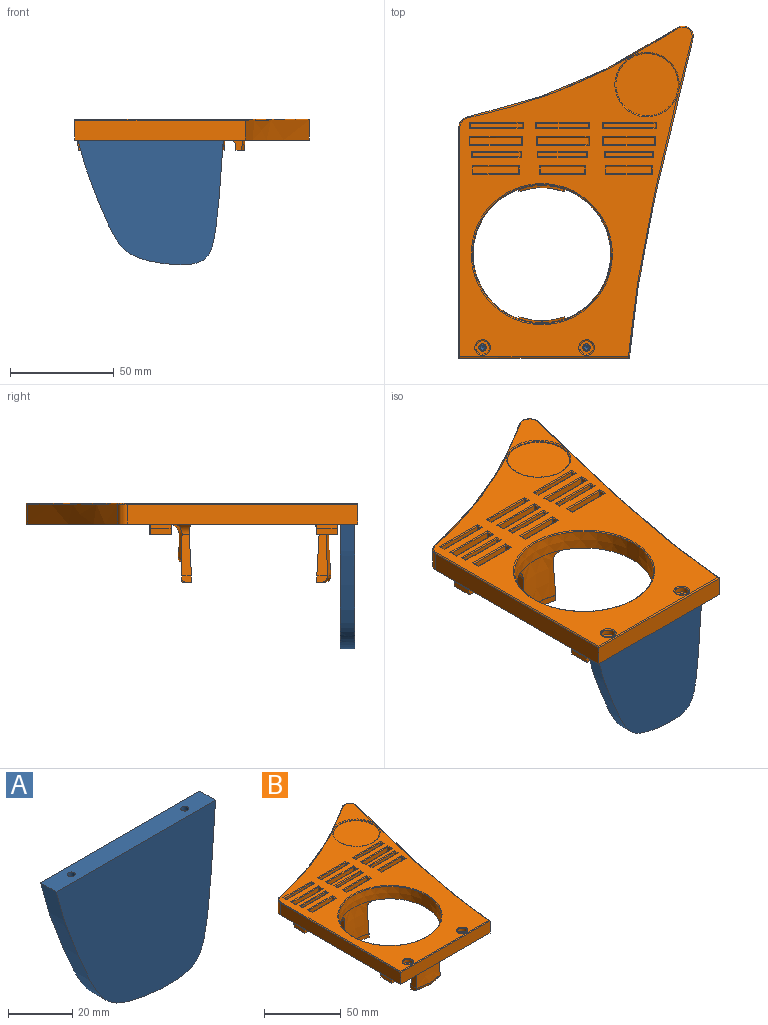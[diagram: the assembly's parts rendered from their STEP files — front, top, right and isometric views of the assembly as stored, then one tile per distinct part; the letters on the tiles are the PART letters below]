
ASSEMBLY  parts=2 mates=1
PART A: 8 faces, bbox 70x7x60.8 mm
  f0: plane 70x7mm, normal (0,0,1), area 480.2mm2, adj f1,f2,f3,f5,f7
  f1: extruded ~70x59.97mm, area 1100.6mm2, adj f0,f2,f3
  f2: plane 70x60.83mm, normal (0,-1,0), area 3319.7mm2, adj f0,f1
  f3: plane 70x60.83mm, normal (0,1,0), area 3319.7mm2, adj f0,f1
  f4: cone r=0mm half-angle=59deg, axis (0,0,1), area 5.7mm2, adj f5
  f5: cylinder r=1.25mm len=13.5mm, axis (0,0,1), area 106mm2, adj f0,f4
  f6: cone r=0mm half-angle=59deg, axis (0,0,1), area 5.7mm2, adj f7
  f7: cylinder r=1.25mm len=13.5mm, axis (0,0,1), area 106mm2, adj f0,f6
PART B: 196 faces, bbox 132.4x213.1x39.5 mm
  f0: plane 4.91x3.13mm, normal (-1,0,0), area 13.1mm2, adj f2,f38,f50,f51,f135
  f1: plane 4.91x3.13mm, normal (1,0,0), area 13.1mm2, adj f2,f40,f50,f51,f135
  f2: bspline ~23.11x4.73mm, area 41mm2, adj f0,f1,f51,f135
  f3: plane 158.85x111.92mm, normal (0,0,1), area 6703.7mm2, adj f138,f139,f140,f141,f142,f143,f144,f145
  f4: plane 12.78x3.46mm, normal (0,0,-1), area 1.2mm2, adj f36,f58
  f5: plane 163.02x112.92mm, normal (0,0,-1), area 8307.5mm2, adj f6,f7,f8,f9,f10,f11,f12,f13
  f6: plane 82.2x9.5mm, normal (0,-1,0), area 780.9mm2, adj f5,f7,f12,f142
  f7: extruded ~153.59x30.56mm, area 1489.5mm2, adj f5,f6,f8,f143
  f8: cylinder r=5mm len=9.5mm, axis (0,0,-1), area 113.5mm2, adj f5,f7,f9,f141
  f9: extruded ~101.41x43.16mm, area 1053.3mm2, adj f5,f8,f10,f139
  f10: cylinder r=5mm len=9.5mm, axis (0,0,-1), area 63.5mm2, adj f5,f9,f12,f138
  f11: cone r=33.11mm half-angle=2.3deg, axis (0,0,1), area 1993.2mm2, adj f5,f34,f39,f195
  f12: plane 111.04x9.5mm, normal (-1,0,0), area 1054.9mm2, adj f5,f6,f10,f140
  f13: plane 6x5mm, normal (0,-1,0), area 16.5mm2, adj f5,f14,f16,f17,f62,f64
  f14: plane 10x2mm, normal (-1,0,0), area 20mm2, adj f5,f13,f15,f64
  f15: plane 6x5mm, normal (0,1,0), area 16.5mm2, adj f5,f14,f16,f17,f62,f64
  f16: plane 10x2mm, normal (1,0,0), area 20mm2, adj f13,f15,f17,f62
  f17: plane 10x2.74mm, normal (0,0,-1), area 27.4mm2, adj f13,f15,f16,f64
  f18: plane 6x5mm, normal (0,-1,0), area 16.5mm2, adj f5,f19,f21,f22,f61,f63
  f19: plane 10x2mm, normal (-1,0,0), area 20mm2, adj f5,f18,f20,f63
  f20: plane 6x5mm, normal (0,1,0), area 16.5mm2, adj f5,f19,f21,f22,f61,f63
  f21: plane 10x2mm, normal (1,0,0), area 20mm2, adj f18,f20,f22,f61
  f22: plane 10x2.74mm, normal (0,0,-1), area 27.4mm2, adj f18,f20,f21,f63
  f23: plane 5.99x5mm, normal (-0.07,-1,0), area 16.5mm2, adj f5,f24,f26,f27,f60,f66
  f24: plane 9.98x2mm, normal (-1,0.07,0), area 20mm2, adj f23,f25,f27,f60
  f25: plane 5.99x5mm, normal (0.07,1,0), area 16.5mm2, adj f5,f24,f26,f27,f60,f66
  f26: plane 9.98x2mm, normal (1,-0.07,0), area 20mm2, adj f5,f23,f25,f66
  f27: plane 10.17x3.44mm, normal (0,0,-1), area 27.4mm2, adj f23,f24,f25,f66
  f28: plane 5.95x5mm, normal (-0.12,-0.99,0), area 16.5mm2, adj f5,f29,f31,f32,f59,f65
  f29: plane 9.92x2mm, normal (-0.99,0.12,0), area 20mm2, adj f28,f30,f32,f59
  f30: plane 5.95x5mm, normal (0.12,0.99,0), area 16.5mm2, adj f5,f29,f31,f32,f59,f65
  f31: plane 9.92x2mm, normal (0.99,-0.12,0), area 20mm2, adj f5,f28,f30,f65
  f32: plane 10.26x3.95mm, normal (0,0,-1), area 27.4mm2, adj f28,f29,f30,f65
  f33: plane 19.82x5.13mm, normal (1,0,0.04), area 84.6mm2, adj f34,f36,f45,f55
  f34: cone r=33.11mm half-angle=2.3deg, axis (0,0,1), area 547.4mm2, adj f11,f33,f35,f42,f43,f55,f57
  f35: plane 19.82x5.13mm, normal (-1,0,0.04), area 84.6mm2, adj f34,f36,f46,f57
  f36: cone r=35.98mm half-angle=2.3deg, axis (0,0,-1), area 426mm2, adj f4,f33,f35,f37,f56
  f37: plane 12.76x3.44mm, normal (0,0,-1), area 1.2mm2, adj f36,f58
  f38: plane 19.9x4.98mm, normal (-1,0,0.04), area 83mm2, adj f0,f39,f41,f52,f135,f136,f137
  f39: cone r=33.11mm half-angle=2.3deg, axis (0,0,1), area 547.4mm2, adj f11,f38,f40,f48,f49,f52,f54
  f40: plane 19.9x4.98mm, normal (1,0,0.04), area 83mm2, adj f1,f39,f41,f54,f135,f136,f137
  f41: cone r=35.98mm half-angle=2.3deg, axis (0,0,-1), area 254.5mm2, adj f38,f40,f53,f137
  f42: plane 11.32x2.27mm, normal (0,0,1), area 1.4mm2, adj f34,f44
  f43: plane 11.32x2.27mm, normal (0,0,1), area 1.4mm2, adj f34,f44
  f44: extruded ~21.97x3mm, area 67.1mm2, adj f42,f43,f45,f46,f47
  f45: plane 5.25x3.14mm, normal (1,0,0), area 13.4mm2, adj f33,f44,f47,f58
  f46: plane 5.24x3.13mm, normal (-1,0,0), area 13.4mm2, adj f35,f44,f47,f58
  f47: plane 21.98x3.78mm, normal (0,0,-1), area 42mm2, adj f44,f45,f46,f58
  f48: plane 11.32x2.27mm, normal (0,0,1), area 1.4mm2, adj f39,f50
  f49: plane 11.32x2.27mm, normal (0,0,1), area 1.4mm2, adj f39,f50
  f50: extruded ~21.97x3mm, area 67.1mm2, adj f0,f1,f48,f49,f51
  f51: plane 21.98x3.78mm, normal (0,0,-1), area 42mm2, adj f0,f1,f2,f50
  f52: cylinder r=5mm len=8.86mm, axis (0,1,0), area 49.5mm2, adj f5,f38,f39,f53
  f53: torus R=41.18mm, axis (0,0,1), area 196.2mm2, adj f5,f41,f52,f54
  f54: cylinder r=5mm len=8.86mm, axis (0,1,0), area 49.5mm2, adj f5,f39,f40,f53
  f55: cylinder r=5mm len=8.86mm, axis (0,-1,0), area 49.5mm2, adj f5,f33,f34,f56
  f56: torus R=41.18mm, axis (0,0,1), area 196.2mm2, adj f5,f36,f55,f57
  f57: cylinder r=5mm len=8.86mm, axis (0,-1,0), area 49.5mm2, adj f5,f34,f35,f56
  f58: bspline ~23.11x4.73mm, area 105.3mm2, adj f4,f37,f45,f46,f47
  f59: cylinder r=3mm len=10.29mm, axis (-0.12,-0.99,0), area 47.1mm2, adj f5,f28,f29,f30
  f60: cylinder r=3mm len=10.19mm, axis (-0.07,-1,0), area 47.1mm2, adj f5,f23,f24,f25
  f61: cylinder r=3mm len=10mm, axis (0,1,0), area 47.1mm2, adj f5,f18,f20,f21
  f62: cylinder r=3mm len=10mm, axis (0,1,0), area 47.1mm2, adj f5,f13,f15,f16
  f63: plane 10x3mm, normal (-1,0,-0.09), area 30.1mm2, adj f18,f19,f20,f22
  f64: plane 10x3mm, normal (-1,0,-0.09), area 30.1mm2, adj f13,f14,f15,f17
  f65: plane 9.96x3mm, normal (0.99,-0.12,-0.09), area 30.1mm2, adj f28,f30,f31,f32
  f66: plane 9.99x3mm, normal (0.99,-0.07,-0.09), area 30.1mm2, adj f23,f25,f26,f27
  f67: cylinder r=1.8mm len=7mm, axis (0,0,1), area 79.2mm2, adj f5,f68
  f68: plane 6.5x6.5mm, normal (0,0,1), area 23mm2, adj f67,f69
  f69: cylinder r=3.25mm len=6.5mm, axis (0,0,1), area 51.1mm2, adj f68,f193
  f70: cylinder r=1.8mm len=7mm, axis (0,0,1), area 79.2mm2, adj f5,f71
  f71: plane 6.5x6.5mm, normal (0,0,1), area 23mm2, adj f70,f72
  f72: cylinder r=3.25mm len=6.5mm, axis (0,0,1), area 51.1mm2, adj f71,f194
  f73: plane 7.5x2.15mm, normal (1,0,0), area 16.1mm2, adj f74,f76,f77,f190
  f74: plane 23x7.5mm, normal (0,1,0), area 172.5mm2, adj f73,f75,f77,f192
  f75: plane 7.5x2.15mm, normal (-1,0,0), area 16.1mm2, adj f74,f76,f77,f191
  f76: plane 23x7.5mm, normal (0,-1,0), area 172.5mm2, adj f73,f75,f77,f189
  f77: plane 23x2.15mm, normal (0,0,1), area 49.4mm2, adj f73,f74,f75,f76
  f78: plane 21.5x7.5mm, normal (0,-1,0), area 161.2mm2, adj f79,f81,f82,f146
  f79: plane 7.5x3.2mm, normal (1,0,0), area 24mm2, adj f78,f80,f82,f148
  f80: plane 21.5x7.5mm, normal (0,1,0), area 161.2mm2, adj f79,f81,f82,f147
  f81: plane 7.5x3.2mm, normal (-1,0,0), area 24mm2, adj f78,f80,f82,f145
  f82: plane 21.5x3.2mm, normal (0,0,1), area 68.8mm2, adj f78,f79,f80,f81
  f83: plane 25x7.5mm, normal (0,-1,0), area 187.5mm2, adj f84,f86,f87,f150
  f84: plane 7.5x2.23mm, normal (1,0,0), area 16.7mm2, adj f83,f85,f87,f152
  f85: plane 25x7.5mm, normal (0,1,0), area 187.5mm2, adj f84,f86,f87,f151
  f86: plane 7.5x2.23mm, normal (-1,0,0), area 16.7mm2, adj f83,f85,f87,f149
  f87: plane 25x2.23mm, normal (0,0,1), area 55.8mm2, adj f83,f84,f85,f86
  f88: plane 24.5x7.5mm, normal (0,-1,0), area 183.7mm2, adj f89,f91,f92,f154
  f89: plane 7.5x3.46mm, normal (1,0,0), area 26mm2, adj f88,f90,f92,f156
  f90: plane 24.5x7.5mm, normal (0,1,0), area 183.7mm2, adj f89,f91,f92,f155
  f91: plane 7.5x3.46mm, normal (-1,0,0), area 26mm2, adj f88,f90,f92,f153
  f92: plane 24.5x3.46mm, normal (0,0,1), area 84.8mm2, adj f88,f89,f90,f91
  f93: plane 24.5x7.5mm, normal (0,-1,0), area 183.7mm2, adj f94,f96,f97,f185
  f94: plane 7.5x3.46mm, normal (1,0,0), area 26mm2, adj f93,f95,f97,f186
  f95: plane 24.5x7.5mm, normal (0,1,0), area 183.7mm2, adj f94,f96,f97,f188
  f96: plane 7.5x3.46mm, normal (-1,0,0), area 26mm2, adj f93,f95,f97,f187
  f97: plane 24.5x3.46mm, normal (0,0,1), area 84.8mm2, adj f93,f94,f95,f96
  f98: plane 25x7.5mm, normal (0,-1,0), area 187.5mm2, adj f99,f101,f102,f182
  f99: plane 7.5x2.23mm, normal (1,0,0), area 16.7mm2, adj f98,f100,f102,f184
  f100: plane 25x7.5mm, normal (0,1,0), area 187.5mm2, adj f99,f101,f102,f183
  f101: plane 7.5x2.23mm, normal (-1,0,0), area 16.7mm2, adj f98,f100,f102,f181
  f102: plane 25x2.23mm, normal (0,0,1), area 55.8mm2, adj f98,f99,f100,f101
  f103: plane 21.5x7.5mm, normal (0,-1,0), area 161.2mm2, adj f104,f106,f107,f178
  f104: plane 7.5x3.2mm, normal (1,0,0), area 24mm2, adj f103,f105,f107,f180
  f105: plane 21.5x7.5mm, normal (0,1,0), area 161.2mm2, adj f104,f106,f107,f179
  f106: plane 7.5x3.2mm, normal (-1,0,0), area 24mm2, adj f103,f105,f107,f177
  f107: plane 21.5x3.2mm, normal (0,0,1), area 68.8mm2, adj f103,f104,f105,f106
  f108: plane 7.5x2.15mm, normal (1,0,0), area 16.1mm2, adj f109,f111,f112,f174
  f109: plane 23x7.5mm, normal (0,1,0), area 172.5mm2, adj f108,f110,f112,f176
  f110: plane 7.5x2.15mm, normal (-1,0,0), area 16.1mm2, adj f109,f111,f112,f175
  f111: plane 23x7.5mm, normal (0,-1,0), area 172.5mm2, adj f108,f110,f112,f173
  f112: plane 23x2.15mm, normal (0,0,1), area 49.4mm2, adj f108,f109,f110,f111
  f113: plane 24.5x7.5mm, normal (0,-1,0), area 183.7mm2, adj f114,f116,f117,f170
  f114: plane 7.5x3.46mm, normal (1,0,0), area 26mm2, adj f113,f115,f117,f172
  f115: plane 24.5x7.5mm, normal (0,1,0), area 183.7mm2, adj f114,f116,f117,f171
  f116: plane 7.5x3.46mm, normal (-1,0,0), area 26mm2, adj f113,f115,f117,f169
  f117: plane 24.5x3.46mm, normal (0,0,1), area 84.8mm2, adj f113,f114,f115,f116
  f118: plane 25x7.5mm, normal (0,-1,0), area 187.5mm2, adj f119,f121,f122,f166
  f119: plane 7.5x2.23mm, normal (1,0,0), area 16.7mm2, adj f118,f120,f122,f168
  f120: plane 25x7.5mm, normal (0,1,0), area 187.5mm2, adj f119,f121,f122,f167
  f121: plane 7.5x2.23mm, normal (-1,0,0), area 16.7mm2, adj f118,f120,f122,f165
  f122: plane 25x2.23mm, normal (0,0,1), area 55.8mm2, adj f118,f119,f120,f121
  f123: plane 21.5x7.5mm, normal (0,-1,0), area 161.2mm2, adj f124,f126,f127,f162
  f124: plane 7.5x3.2mm, normal (1,0,0), area 24mm2, adj f123,f125,f127,f164
  f125: plane 21.5x7.5mm, normal (0,1,0), area 161.2mm2, adj f124,f126,f127,f163
  f126: plane 7.5x3.2mm, normal (-1,0,0), area 24mm2, adj f123,f125,f127,f161
  f127: plane 21.5x3.2mm, normal (0,0,1), area 68.8mm2, adj f123,f124,f125,f126
  f128: plane 7.5x2.15mm, normal (1,0,0), area 16.1mm2, adj f129,f131,f132,f158
  f129: plane 23x7.5mm, normal (0,1,0), area 172.5mm2, adj f128,f130,f132,f160
  f130: plane 7.5x2.15mm, normal (-1,0,0), area 16.1mm2, adj f129,f131,f132,f159
  f131: plane 23x7.5mm, normal (0,-1,0), area 172.5mm2, adj f128,f130,f132,f157
  f132: plane 23x2.15mm, normal (0,0,1), area 49.4mm2, adj f128,f129,f130,f131
  f133: cylinder r=15mm len=30mm, axis (0,0,1), area 47.1mm2, adj f134,f144
  f134: plane 30x30mm, normal (0,0,1), area 706.9mm2, adj f133
  f135: plane 21.98x9.5mm, normal (0,1,0), area 177.7mm2, adj f0,f1,f2,f38,f40,f136
  f136: bspline ~22.16x1.98mm, area 32.5mm2, adj f38,f40,f135,f137
  f137: bspline ~22.26x1.78mm, area 34.4mm2, adj f38,f40,f41,f136
  f138: torus R=4.5mm, axis (0,0,1), area 5.1mm2, adj f3,f10,f139,f140
  f139: bspline ~130.97x59.64mm, area 87.1mm2, adj f3,f9,f138,f141
  f140: cylinder r=0.5mm len=111.04mm, axis (0,1,0), area 87mm2, adj f3,f12,f138,f142
  f141: torus R=4.5mm, axis (0,0,1), area 9mm2, adj f3,f8,f139,f143
  f142: cylinder r=0.5mm len=82.2mm, axis (-1,0,0), area 64.2mm2, adj f3,f6,f140,f143
  f143: bspline ~211.6x45.07mm, area 123mm2, adj f3,f7,f141,f142,f144
  f144: torus R=15.5mm, axis (0,0,1), area 74.9mm2, adj f3,f133,f143
  f145: cylinder r=0.5mm len=4.2mm, axis (0,-1,0), area 2.9mm2, adj f3,f81,f146,f147
  f146: cylinder r=0.5mm len=22.5mm, axis (1,0,0), area 17.3mm2, adj f3,f78,f145,f148
  f147: cylinder r=0.5mm len=22.5mm, axis (-1,0,0), area 17.3mm2, adj f3,f80,f145,f148
  f148: cylinder r=0.5mm len=4.2mm, axis (0,1,0), area 2.9mm2, adj f3,f79,f146,f147
  f149: cylinder r=0.5mm len=3.23mm, axis (0,-1,0), area 2.1mm2, adj f3,f86,f150,f151
  f150: cylinder r=0.5mm len=26mm, axis (1,0,0), area 20mm2, adj f3,f83,f149,f152
  f151: cylinder r=0.5mm len=26mm, axis (-1,0,0), area 20mm2, adj f3,f85,f149,f152
  f152: cylinder r=0.5mm len=3.23mm, axis (0,1,0), area 2.1mm2, adj f3,f84,f150,f151
  f153: cylinder r=0.5mm len=4.46mm, axis (0,-1,0), area 3.1mm2, adj f3,f91,f154,f155
  f154: cylinder r=0.5mm len=25.5mm, axis (1,0,0), area 19.6mm2, adj f3,f88,f153,f156
  f155: cylinder r=0.5mm len=25.5mm, axis (-1,0,0), area 19.6mm2, adj f3,f90,f153,f156
  f156: cylinder r=0.5mm len=4.46mm, axis (0,1,0), area 3.1mm2, adj f3,f89,f154,f155
  f157: cylinder r=0.5mm len=24mm, axis (1,0,0), area 18.5mm2, adj f3,f131,f158,f159
  f158: cylinder r=0.5mm len=3.15mm, axis (0,1,0), area 2.1mm2, adj f3,f128,f157,f160
  f159: cylinder r=0.5mm len=3.15mm, axis (0,-1,0), area 2.1mm2, adj f3,f130,f157,f160
  f160: cylinder r=0.5mm len=24mm, axis (-1,0,0), area 18.5mm2, adj f3,f129,f158,f159
  f161: cylinder r=0.5mm len=4.2mm, axis (0,-1,0), area 2.9mm2, adj f3,f126,f162,f163
  f162: cylinder r=0.5mm len=22.5mm, axis (1,0,0), area 17.3mm2, adj f3,f123,f161,f164
  f163: cylinder r=0.5mm len=22.5mm, axis (-1,0,0), area 17.3mm2, adj f3,f125,f161,f164
  f164: cylinder r=0.5mm len=4.2mm, axis (0,1,0), area 2.9mm2, adj f3,f124,f162,f163
  f165: cylinder r=0.5mm len=3.23mm, axis (0,-1,0), area 2.1mm2, adj f3,f121,f166,f167
  f166: cylinder r=0.5mm len=26mm, axis (1,0,0), area 20mm2, adj f3,f118,f165,f168
  f167: cylinder r=0.5mm len=26mm, axis (-1,0,0), area 20mm2, adj f3,f120,f165,f168
  f168: cylinder r=0.5mm len=3.23mm, axis (0,1,0), area 2.1mm2, adj f3,f119,f166,f167
  f169: cylinder r=0.5mm len=4.46mm, axis (0,-1,0), area 3.1mm2, adj f3,f116,f170,f171
  f170: cylinder r=0.5mm len=25.5mm, axis (1,0,0), area 19.6mm2, adj f3,f113,f169,f172
  f171: cylinder r=0.5mm len=25.5mm, axis (-1,0,0), area 19.6mm2, adj f3,f115,f169,f172
  f172: cylinder r=0.5mm len=4.46mm, axis (0,1,0), area 3.1mm2, adj f3,f114,f170,f171
  f173: cylinder r=0.5mm len=24mm, axis (1,0,0), area 18.5mm2, adj f3,f111,f174,f175
  f174: cylinder r=0.5mm len=3.15mm, axis (0,1,0), area 2.1mm2, adj f3,f108,f173,f176
  f175: cylinder r=0.5mm len=3.15mm, axis (0,-1,0), area 2.1mm2, adj f3,f110,f173,f176
  f176: cylinder r=0.5mm len=24mm, axis (-1,0,0), area 18.5mm2, adj f3,f109,f174,f175
  f177: cylinder r=0.5mm len=4.2mm, axis (0,-1,0), area 2.9mm2, adj f3,f106,f178,f179
  f178: cylinder r=0.5mm len=22.5mm, axis (1,0,0), area 17.3mm2, adj f3,f103,f177,f180
  f179: cylinder r=0.5mm len=22.5mm, axis (-1,0,0), area 17.3mm2, adj f3,f105,f177,f180
  f180: cylinder r=0.5mm len=4.2mm, axis (0,1,0), area 2.9mm2, adj f3,f104,f178,f179
  f181: cylinder r=0.5mm len=3.23mm, axis (0,-1,0), area 2.1mm2, adj f3,f101,f182,f183
  f182: cylinder r=0.5mm len=26mm, axis (1,0,0), area 20mm2, adj f3,f98,f181,f184
  f183: cylinder r=0.5mm len=26mm, axis (-1,0,0), area 20mm2, adj f3,f100,f181,f184
  f184: cylinder r=0.5mm len=3.23mm, axis (0,1,0), area 2.1mm2, adj f3,f99,f182,f183
  f185: cylinder r=0.5mm len=25.5mm, axis (1,0,0), area 19.6mm2, adj f3,f93,f186,f187
  f186: cylinder r=0.5mm len=4.46mm, axis (0,1,0), area 3.1mm2, adj f3,f94,f185,f188
  f187: cylinder r=0.5mm len=4.46mm, axis (0,-1,0), area 3.1mm2, adj f3,f96,f185,f188
  f188: cylinder r=0.5mm len=25.5mm, axis (-1,0,0), area 19.6mm2, adj f3,f95,f186,f187
  f189: cylinder r=0.5mm len=24mm, axis (1,0,0), area 18.5mm2, adj f3,f76,f190,f191
  f190: cylinder r=0.5mm len=3.15mm, axis (0,1,0), area 2.1mm2, adj f3,f73,f189,f192
  f191: cylinder r=0.5mm len=3.15mm, axis (0,-1,0), area 2.1mm2, adj f3,f75,f189,f192
  f192: cylinder r=0.5mm len=24mm, axis (-1,0,0), area 18.5mm2, adj f3,f74,f190,f191
  f193: torus R=3.75mm, axis (0,0,1), area 16.9mm2, adj f3,f69
  f194: torus R=3.75mm, axis (0,0,1), area 16.9mm2, adj f3,f72
  f195: torus R=33.99mm, axis (0,0,1), area 162mm2, adj f3,f11
PLACE A t=(5.19,44.5,-29.02)mm
PLACE B t=(3.69,-9,-29.02)mm
MATE fastened A.f4 <-> B.f67  axis (0,0,1) through (15.19,41,-29.02)mm
